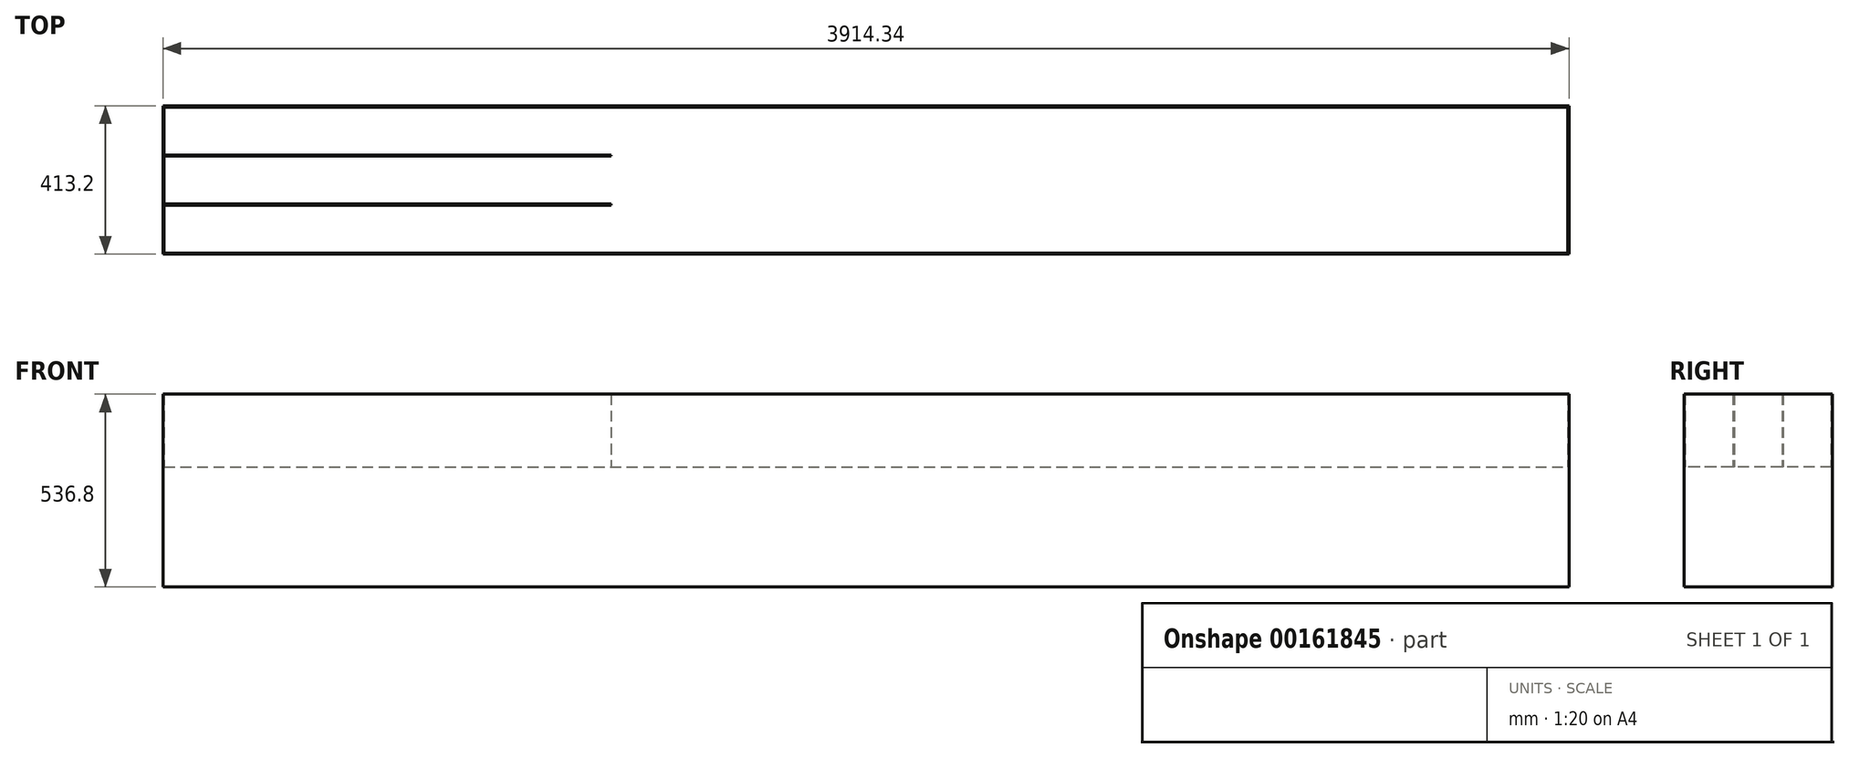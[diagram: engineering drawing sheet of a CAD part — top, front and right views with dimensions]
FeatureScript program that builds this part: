
annotation { "Feature Type Name" : "Feature", "Feature Type Description" : "" }
export const myFeature = defineFeature(function(context is Context, id is Id, definition is map)
    precondition{}
    {
        {
            var Q0;
            Q0=qCreatedBy(makeId("Top.planeOp"),FACE);
            var sketch = newSketch(context, id + "F0", { "sketchPlane" : qUnion([Q0])});
            skLineSegment(sketch, "E0.bottom", {"start": v(-1953.77, 203.2) * mm, "end": v(1953.77, 203.2) * mm});
            skLineSegment(sketch, "E0.top", {"start": v(-1953.77, -203.2) * mm, "end": v(1953.77, -203.2) * mm});
            skLineSegment(sketch, "E0.left", {"start": v(-1953.77, 203.2) * mm, "end": v(-1953.77, -203.2) * mm});
            skLineSegment(sketch, "E0.right", {"start": v(1953.77, 203.2) * mm, "end": v(1953.77, -203.2) * mm});
            skPoint(sketch, "E0.middle", {"position": v(0, 0) * mm});
            skLineSegment(sketch, "E1.bottom", {"start": v(-709.17, 203.2) * mm, "end": v(-705.76, 203.2) * mm});
            skLineSegment(sketch, "E1.top", {"start": v(-709.17, -203.2) * mm, "end": v(-705.76, -203.2) * mm});
            skLineSegment(sketch, "E1.left", {"start": v(-709.17, 203.2) * mm, "end": v(-709.17, -203.2) * mm});
            skLineSegment(sketch, "E1.right", {"start": v(-705.76, 203.2) * mm, "end": v(-705.76, -203.2) * mm});
            skLineSegment(sketch, "E2.bottom", {"start": v(-1953.77, 69.85) * mm, "end": v(-709.17, 69.85) * mm});
            skLineSegment(sketch, "E2.top", {"start": v(-1953.77, 66.45) * mm, "end": v(-709.17, 66.45) * mm});
            skLineSegment(sketch, "E2.left", {"start": v(-1953.77, 69.85) * mm, "end": v(-1953.77, 66.45) * mm});
            skLineSegment(sketch, "E2.right", {"start": v(-709.17, 69.85) * mm, "end": v(-709.17, 66.45) * mm});
            skLineSegment(sketch, "E3.bottom", {"start": v(-1953.77, -66.9) * mm, "end": v(-709.17, -66.9) * mm});
            skLineSegment(sketch, "E3.top", {"start": v(-1953.77, -70.3) * mm, "end": v(-709.17, -70.3) * mm});
            skLineSegment(sketch, "E3.left", {"start": v(-1953.77, -66.9) * mm, "end": v(-1953.77, -70.3) * mm});
            skLineSegment(sketch, "E3.right", {"start": v(-709.17, -66.9) * mm, "end": v(-709.17, -70.3) * mm});
            skLineSegment(sketch, "E4.bottom", {"start": v(-311.15, 203.2) * mm, "end": v(-307.75, 203.2) * mm});
            skLineSegment(sketch, "E4.top", {"start": v(-311.15, -203.2) * mm, "end": v(-307.75, -203.2) * mm});
            skLineSegment(sketch, "E4.left", {"start": v(-311.15, 203.2) * mm, "end": v(-311.15, -203.2) * mm});
            skLineSegment(sketch, "E4.right", {"start": v(-307.75, 203.2) * mm, "end": v(-307.75, -203.2) * mm});
            skLineSegment(sketch, "E5.bottom", {"start": v(-705.76, 0) * mm, "end": v(-311.15, 0) * mm});
            skLineSegment(sketch, "E5.top", {"start": v(-705.76, -3.4) * mm, "end": v(-311.15, -3.4) * mm});
            skLineSegment(sketch, "E5.left", {"start": v(-705.76, 0) * mm, "end": v(-705.76, -3.4) * mm});
            skLineSegment(sketch, "E5.right", {"start": v(-311.15, 0) * mm, "end": v(-311.15, -3.4) * mm});
            skLineSegment(sketch, "E6.bottom", {"start": v(-629.56, 203.2) * mm, "end": v(-626.16, 203.2) * mm});
            skLineSegment(sketch, "E6.top", {"start": v(-629.56, 0) * mm, "end": v(-626.16, 0) * mm});
            skLineSegment(sketch, "E6.left", {"start": v(-629.56, 203.2) * mm, "end": v(-629.56, 0) * mm});
            skLineSegment(sketch, "E6.right", {"start": v(-626.16, 203.2) * mm, "end": v(-626.16, 0) * mm});
            skLineSegment(sketch, "E7.bottom", {"start": v(-629.56, -3.4) * mm, "end": v(-626.16, -3.4) * mm});
            skLineSegment(sketch, "E7.top", {"start": v(-629.56, -203.2) * mm, "end": v(-626.16, -203.2) * mm});
            skLineSegment(sketch, "E7.left", {"start": v(-629.56, -3.4) * mm, "end": v(-629.56, -203.2) * mm});
            skLineSegment(sketch, "E7.right", {"start": v(-626.16, -3.4) * mm, "end": v(-626.16, -203.2) * mm});
            skLineSegment(sketch, "E8.bottom", {"start": v(-549.96, 203.2) * mm, "end": v(-546.56, 203.2) * mm});
            skLineSegment(sketch, "E8.top", {"start": v(-549.96, 0) * mm, "end": v(-546.56, 0) * mm});
            skLineSegment(sketch, "E8.left", {"start": v(-549.96, 203.2) * mm, "end": v(-549.96, 0) * mm});
            skLineSegment(sketch, "E8.right", {"start": v(-546.56, 203.2) * mm, "end": v(-546.56, 0) * mm});
            skLineSegment(sketch, "E9.bottom", {"start": v(-549.96, -3.4) * mm, "end": v(-546.56, -3.4) * mm});
            skLineSegment(sketch, "E9.top", {"start": v(-549.96, -203.2) * mm, "end": v(-546.56, -203.2) * mm});
            skLineSegment(sketch, "E9.left", {"start": v(-549.96, -3.4) * mm, "end": v(-549.96, -203.2) * mm});
            skLineSegment(sketch, "E9.right", {"start": v(-546.56, -3.4) * mm, "end": v(-546.56, -203.2) * mm});
            skLineSegment(sketch, "E10.bottom", {"start": v(-470.36, 203.2) * mm, "end": v(-466.95, 203.2) * mm});
            skLineSegment(sketch, "E10.top", {"start": v(-470.36, 0) * mm, "end": v(-466.95, 0) * mm});
            skLineSegment(sketch, "E10.left", {"start": v(-470.36, 203.2) * mm, "end": v(-470.36, 0) * mm});
            skLineSegment(sketch, "E10.right", {"start": v(-466.95, 203.2) * mm, "end": v(-466.95, 0) * mm});
            skLineSegment(sketch, "E11.bottom", {"start": v(-470.36, -3.4) * mm, "end": v(-466.95, -3.4) * mm});
            skLineSegment(sketch, "E11.top", {"start": v(-470.36, -203.2) * mm, "end": v(-466.95, -203.2) * mm});
            skLineSegment(sketch, "E11.left", {"start": v(-470.36, -3.4) * mm, "end": v(-470.36, -203.2) * mm});
            skLineSegment(sketch, "E11.right", {"start": v(-466.95, -3.4) * mm, "end": v(-466.95, -203.2) * mm});
            skLineSegment(sketch, "E12.bottom", {"start": v(-390.75, 203.2) * mm, "end": v(-387.35, 203.2) * mm});
            skLineSegment(sketch, "E12.top", {"start": v(-390.75, 0) * mm, "end": v(-387.35, 0) * mm});
            skLineSegment(sketch, "E12.left", {"start": v(-390.75, 203.2) * mm, "end": v(-390.75, 0) * mm});
            skLineSegment(sketch, "E12.right", {"start": v(-387.35, 203.2) * mm, "end": v(-387.35, 0) * mm});
            skLineSegment(sketch, "E13.bottom", {"start": v(-390.75, -3.4) * mm, "end": v(-387.35, -3.4) * mm});
            skLineSegment(sketch, "E13.top", {"start": v(-390.75, -203.2) * mm, "end": v(-387.35, -203.2) * mm});
            skLineSegment(sketch, "E13.left", {"start": v(-390.75, -3.4) * mm, "end": v(-390.75, -203.2) * mm});
            skLineSegment(sketch, "E13.right", {"start": v(-387.35, -3.4) * mm, "end": v(-387.35, -203.2) * mm});
            skLineSegment(sketch, "E14.bottom", {"start": v(-307.75, 0) * mm, "end": v(1953.77, 0) * mm});
            skLineSegment(sketch, "E14.top", {"start": v(-307.75, -3.4) * mm, "end": v(1953.77, -3.4) * mm});
            skLineSegment(sketch, "E14.left", {"start": v(-307.75, 0) * mm, "end": v(-307.75, -3.4) * mm});
            skLineSegment(sketch, "E14.right", {"start": v(1953.77, 0) * mm, "end": v(1953.77, -3.4) * mm});
            skLineSegment(sketch, "E15.bottom", {"start": v(-180.75, 203.2) * mm, "end": v(-177.34, 203.2) * mm});
            skLineSegment(sketch, "E15.top", {"start": v(-180.75, 0) * mm, "end": v(-177.34, 0) * mm});
            skLineSegment(sketch, "E15.left", {"start": v(-180.75, 203.2) * mm, "end": v(-180.75, 0) * mm});
            skLineSegment(sketch, "E15.right", {"start": v(-177.34, 203.2) * mm, "end": v(-177.34, 0) * mm});
            skLineSegment(sketch, "E16.bottom", {"start": v(279.86, 203.2) * mm, "end": v(283.26, 203.2) * mm});
            skLineSegment(sketch, "E16.top", {"start": v(279.86, 0) * mm, "end": v(283.26, 0) * mm});
            skLineSegment(sketch, "E16.left", {"start": v(279.86, 203.2) * mm, "end": v(279.86, 0) * mm});
            skLineSegment(sketch, "E16.right", {"start": v(283.26, 203.2) * mm, "end": v(283.26, 0) * mm});
            skLineSegment(sketch, "E17.bottom", {"start": v(562.66, 203.2) * mm, "end": v(566.06, 203.2) * mm});
            skLineSegment(sketch, "E17.top", {"start": v(562.66, 0) * mm, "end": v(566.06, 0) * mm});
            skLineSegment(sketch, "E17.left", {"start": v(562.66, 203.2) * mm, "end": v(562.66, 0) * mm});
            skLineSegment(sketch, "E17.right", {"start": v(566.06, 203.2) * mm, "end": v(566.06, 0) * mm});
            skLineSegment(sketch, "E18.bottom", {"start": v(896.26, 203.2) * mm, "end": v(899.67, 203.2) * mm});
            skLineSegment(sketch, "E18.top", {"start": v(896.26, 0) * mm, "end": v(899.67, 0) * mm});
            skLineSegment(sketch, "E18.left", {"start": v(896.26, 203.2) * mm, "end": v(896.26, 0) * mm});
            skLineSegment(sketch, "E18.right", {"start": v(899.67, 203.2) * mm, "end": v(899.67, 0) * mm});
            skLineSegment(sketch, "E19.bottom", {"start": v(225.65, -3.4) * mm, "end": v(229.06, -3.4) * mm});
            skLineSegment(sketch, "E19.top", {"start": v(225.65, -203.2) * mm, "end": v(229.06, -203.2) * mm});
            skLineSegment(sketch, "E19.left", {"start": v(225.65, -3.4) * mm, "end": v(225.65, -203.2) * mm});
            skLineSegment(sketch, "E19.right", {"start": v(229.06, -3.4) * mm, "end": v(229.06, -203.2) * mm});
            skLineSegment(sketch, "E20.bottom", {"start": v(566.06, -3.4) * mm, "end": v(562.66, -3.4) * mm});
            skLineSegment(sketch, "E20.top", {"start": v(566.06, -203.2) * mm, "end": v(562.66, -203.2) * mm});
            skLineSegment(sketch, "E20.left", {"start": v(566.06, -3.4) * mm, "end": v(566.06, -203.2) * mm});
            skLineSegment(sketch, "E20.right", {"start": v(562.66, -3.4) * mm, "end": v(562.66, -203.2) * mm});
            skLineSegment(sketch, "E21.bottom", {"start": v(896.26, -3.4) * mm, "end": v(899.67, -3.4) * mm});
            skLineSegment(sketch, "E21.top", {"start": v(896.26, -203.2) * mm, "end": v(899.67, -203.2) * mm});
            skLineSegment(sketch, "E21.left", {"start": v(896.26, -3.4) * mm, "end": v(896.26, -203.2) * mm});
            skLineSegment(sketch, "E21.right", {"start": v(899.67, -3.4) * mm, "end": v(899.67, -203.2) * mm});
            skLineSegment(sketch, "E22.bottom", {"start": v(-1957.17, 206.6) * mm, "end": v(1957.17, 206.6) * mm});
            skLineSegment(sketch, "E22.top", {"start": v(-1957.17, -206.6) * mm, "end": v(1957.17, -206.6) * mm});
            skLineSegment(sketch, "E22.left", {"start": v(-1957.17, 206.6) * mm, "end": v(-1957.17, -206.6) * mm});
            skLineSegment(sketch, "E22.right", {"start": v(1957.17, 206.6) * mm, "end": v(1957.17, -206.6) * mm});
            skSolve(sketch);
        }
        {
            var Q0;
            Q0 = qSketchRegion(id + "F0", true);
            var Q1;
            Q1=makeQuery(id+"F0.imprint","IMPRINT",FACE,{"disambiguationData":[TD([[makeQuery(id+"F0.imprint","IMPRINT",EDGE,{"derivedFrom":sQuery(id+"F0.wireOp",EDGE,"E2.bottom")}),-1.0]])]});
            var Q2;
            Q2=makeQuery(id+"F0.imprint","IMPRINT",FACE,{"disambiguationData":[TD([[makeQuery(id+"F0.imprint","IMPRINT",EDGE,{"derivedFrom":sQuery(id+"F0.wireOp",EDGE,"E3.bottom")}),-1.0]])]});
            var Q3;
            {var subQ3=sQuery(id+"F0.wireOp",EDGE,"E1.bottom");Q3=makeQuery(id+"F0.imprint","IMPRINT",FACE,{"disambiguationData":[TD([[makeQuery(id+"F0.imprint","IMPRINT",EDGE,{"derivedFrom":subQ3}),-1.0]])]});}
            var Q4;
            {var subQ7=sQuery(id+"F0.wireOp",EDGE,"E5.left");Q4=makeQuery(id+"F0.imprint","IMPRINT",FACE,{"disambiguationData":[TD([[makeQuery(id+"F0.imprint","IMPRINT",EDGE,{"derivedFrom":subQ7}),1.0]])]});}
            var Q5;
            Q5=makeQuery(id+"F0.imprint","IMPRINT",FACE,{"disambiguationData":[TD([[makeQuery(id+"F0.imprint","IMPRINT",EDGE,{"derivedFrom":sQuery(id+"F0.wireOp",EDGE,"E6.bottom")}),-1.0]])]});
            var Q6;
            Q6=makeQuery(id+"F0.imprint","IMPRINT",FACE,{"disambiguationData":[TD([[makeQuery(id+"F0.imprint","IMPRINT",EDGE,{"derivedFrom":sQuery(id+"F0.wireOp",EDGE,"E7.bottom")}),-1.0]])]});
            var Q7;
            Q7=makeQuery(id+"F0.imprint","IMPRINT",FACE,{"disambiguationData":[TD([[makeQuery(id+"F0.imprint","IMPRINT",EDGE,{"derivedFrom":sQuery(id+"F0.wireOp",EDGE,"E9.bottom")}),-1.0]])]});
            var Q8;
            Q8=makeQuery(id+"F0.imprint","IMPRINT",FACE,{"disambiguationData":[TD([[makeQuery(id+"F0.imprint","IMPRINT",EDGE,{"derivedFrom":sQuery(id+"F0.wireOp",EDGE,"E8.bottom")}),-1.0]])]});
            var Q9;
            Q9=makeQuery(id+"F0.imprint","IMPRINT",FACE,{"disambiguationData":[TD([[makeQuery(id+"F0.imprint","IMPRINT",EDGE,{"derivedFrom":sQuery(id+"F0.wireOp",EDGE,"E10.bottom")}),-1.0]])]});
            var Q10;
            Q10=makeQuery(id+"F0.imprint","IMPRINT",FACE,{"disambiguationData":[TD([[makeQuery(id+"F0.imprint","IMPRINT",EDGE,{"derivedFrom":sQuery(id+"F0.wireOp",EDGE,"E11.bottom")}),-1.0]])]});
            var Q11;
            Q11=makeQuery(id+"F0.imprint","IMPRINT",FACE,{"disambiguationData":[TD([[makeQuery(id+"F0.imprint","IMPRINT",EDGE,{"derivedFrom":sQuery(id+"F0.wireOp",EDGE,"E13.bottom")}),-1.0]])]});
            var Q12;
            Q12=makeQuery(id+"F0.imprint","IMPRINT",FACE,{"disambiguationData":[TD([[makeQuery(id+"F0.imprint","IMPRINT",EDGE,{"derivedFrom":sQuery(id+"F0.wireOp",EDGE,"E12.bottom")}),-1.0]])]});
            var Q13;
            {var subQ5=sQuery(id+"F0.wireOp",EDGE,"E4.bottom");Q13=makeQuery(id+"F0.imprint","IMPRINT",FACE,{"disambiguationData":[TD([[makeQuery(id+"F0.imprint","IMPRINT",EDGE,{"derivedFrom":subQ5}),-1.0]])]});}
            var Q14;
            {var subQ0=sQuery(id+"F0.wireOp",EDGE,"E14.left");Q14=makeQuery(id+"F0.imprint","IMPRINT",FACE,{"disambiguationData":[TD([[makeQuery(id+"F0.imprint","IMPRINT",EDGE,{"derivedFrom":subQ0}),1.0]])]});}
            var Q15;
            Q15=makeQuery(id+"F0.imprint","IMPRINT",FACE,{"disambiguationData":[TD([[makeQuery(id+"F0.imprint","IMPRINT",EDGE,{"derivedFrom":sQuery(id+"F0.wireOp",EDGE,"E15.bottom")}),-1.0]])]});
            var Q16;
            Q16=makeQuery(id+"F0.imprint","IMPRINT",FACE,{"disambiguationData":[TD([[makeQuery(id+"F0.imprint","IMPRINT",EDGE,{"derivedFrom":sQuery(id+"F0.wireOp",EDGE,"E16.bottom")}),-1.0]])]});
            var Q17;
            Q17=makeQuery(id+"F0.imprint","IMPRINT",FACE,{"disambiguationData":[TD([[makeQuery(id+"F0.imprint","IMPRINT",EDGE,{"derivedFrom":sQuery(id+"F0.wireOp",EDGE,"E19.bottom")}),-1.0]])]});
            var Q18;
            Q18=makeQuery(id+"F0.imprint","IMPRINT",FACE,{"disambiguationData":[TD([[makeQuery(id+"F0.imprint","IMPRINT",EDGE,{"derivedFrom":sQuery(id+"F0.wireOp",EDGE,"E20.bottom")}),1.0]])]});
            var Q19;
            Q19=makeQuery(id+"F0.imprint","IMPRINT",FACE,{"disambiguationData":[TD([[makeQuery(id+"F0.imprint","IMPRINT",EDGE,{"derivedFrom":sQuery(id+"F0.wireOp",EDGE,"E17.bottom")}),-1.0]])]});
            var Q20;
            Q20=makeQuery(id+"F0.imprint","IMPRINT",FACE,{"disambiguationData":[TD([[makeQuery(id+"F0.imprint","IMPRINT",EDGE,{"derivedFrom":sQuery(id+"F0.wireOp",EDGE,"E18.bottom")}),-1.0]])]});
            var Q21;
            Q21=makeQuery(id+"F0.imprint","IMPRINT",FACE,{"disambiguationData":[TD([[makeQuery(id+"F0.imprint","IMPRINT",EDGE,{"derivedFrom":sQuery(id+"F0.wireOp",EDGE,"E21.bottom")}),-1.0]])]});
            extrude(context, id + "F1", {"entities" : qUnion([Q0, Q1, Q2, Q3, Q4, Q5, Q6, Q7, Q8, Q9, Q10, Q11, Q12, Q13, Q14, Q15, Q16, Q17, Q18, Q19, Q20, Q21]), "depth" : 533.4 * mm});
        }
        {
            var Q0;
            Q0=makeQuery(id+"F1.opExtrude","CAP_FACE",FACE,{"disambiguationData":[OSD([sQuery(id+"F0.wireOp",EDGE,"E0.bottom"),sQuery(id+"F0.wireOp",EDGE,"E0.top"),sQuery(id+"F0.wireOp",EDGE,"E0.left"),sQuery(id+"F0.wireOp",EDGE,"E0.right"),sQuery(id+"F0.wireOp",EDGE,"E1.left"),sQuery(id+"F0.wireOp",EDGE,"E1.right"),sQuery(id+"F0.wireOp",EDGE,"E2.bottom"),sQuery(id+"F0.wireOp",EDGE,"E2.top"),sQuery(id+"F0.wireOp",EDGE,"E3.bottom"),sQuery(id+"F0.wireOp",EDGE,"E3.top"),sQuery(id+"F0.wireOp",EDGE,"E4.left"),sQuery(id+"F0.wireOp",EDGE,"E4.right"),sQuery(id+"F0.wireOp",EDGE,"E5.bottom"),sQuery(id+"F0.wireOp",EDGE,"E5.top"),sQuery(id+"F0.wireOp",EDGE,"E6.left"),sQuery(id+"F0.wireOp",EDGE,"E6.right"),sQuery(id+"F0.wireOp",EDGE,"E7.left"),sQuery(id+"F0.wireOp",EDGE,"E7.right"),sQuery(id+"F0.wireOp",EDGE,"E8.left"),sQuery(id+"F0.wireOp",EDGE,"E8.right"),sQuery(id+"F0.wireOp",EDGE,"E9.left"),sQuery(id+"F0.wireOp",EDGE,"E9.right"),sQuery(id+"F0.wireOp",EDGE,"E10.left"),sQuery(id+"F0.wireOp",EDGE,"E10.right"),sQuery(id+"F0.wireOp",EDGE,"E11.left"),sQuery(id+"F0.wireOp",EDGE,"E11.right"),sQuery(id+"F0.wireOp",EDGE,"E12.left"),sQuery(id+"F0.wireOp",EDGE,"E12.right"),sQuery(id+"F0.wireOp",EDGE,"E13.left"),sQuery(id+"F0.wireOp",EDGE,"E13.right"),sQuery(id+"F0.wireOp",EDGE,"E14.bottom"),sQuery(id+"F0.wireOp",EDGE,"E14.top"),sQuery(id+"F0.wireOp",EDGE,"E15.left"),sQuery(id+"F0.wireOp",EDGE,"E15.right"),sQuery(id+"F0.wireOp",EDGE,"E16.left"),sQuery(id+"F0.wireOp",EDGE,"E16.right"),sQuery(id+"F0.wireOp",EDGE,"E17.left"),sQuery(id+"F0.wireOp",EDGE,"E17.right"),sQuery(id+"F0.wireOp",EDGE,"E18.left"),sQuery(id+"F0.wireOp",EDGE,"E18.right"),sQuery(id+"F0.wireOp",EDGE,"E19.left"),sQuery(id+"F0.wireOp",EDGE,"E19.right"),sQuery(id+"F0.wireOp",EDGE,"E20.left"),sQuery(id+"F0.wireOp",EDGE,"E20.right"),sQuery(id+"F0.wireOp",EDGE,"E21.left"),sQuery(id+"F0.wireOp",EDGE,"E21.right"),sQuery(id+"F0.wireOp",EDGE,"E22.bottom"),sQuery(id+"F0.wireOp",EDGE,"E22.top"),sQuery(id+"F0.wireOp",EDGE,"E22.left"),sQuery(id+"F0.wireOp",EDGE,"E22.right")])],"isStart":true});
            var sketch = newSketch(context, id + "F2", { "sketchPlane" : qUnion([Q0])});
            skLineSegment(sketch, "E23.bottom", {"start": v(-1957.17, 206.6) * mm, "end": v(1957.17, 206.6) * mm});
            skLineSegment(sketch, "E23.top", {"start": v(-1957.17, -206.6) * mm, "end": v(1957.17, -206.6) * mm});
            skLineSegment(sketch, "E23.left", {"start": v(-1957.17, 206.6) * mm, "end": v(-1957.17, -206.6) * mm});
            skLineSegment(sketch, "E23.right", {"start": v(1957.17, 206.6) * mm, "end": v(1957.17, -206.6) * mm});
            skSolve(sketch);
        }
        {
            var Q0;
            Q0 = qSketchRegion(id + "F2", true);
            extrude(context, id + "F3", {"entities" : qUnion([Q0]), "operationType" : NewBodyOperationType.ADD, "depth" : 3.4 * mm});
        }
        {
            var Q0;
            {var subQ5=sQuery(id+"F0.wireOp",EDGE,"E2.bottom");Q0=makeQuery(id+"F3.boolean.opBoolean","SPLIT",FACE,{"disambiguationData":[TD([makeQuery(id+"F1.opExtrude","SWEPT_FACE",FACE,{"disambiguationData":[OSD([subQ5])]})])],"derivedFrom":makeQuery(id+"F3.opExtrude","CAP_FACE",FACE,{"disambiguationData":[OSD([sQuery(id+"F2.wireOp",EDGE,"E23.bottom"),sQuery(id+"F2.wireOp",EDGE,"E23.top"),sQuery(id+"F2.wireOp",EDGE,"E23.left"),sQuery(id+"F2.wireOp",EDGE,"E23.right")])],"isStart":true})});}
            var Q1;
            {var subQ0=sQuery(id+"F0.wireOp",EDGE,"E2.top");Q1=makeQuery(id+"F3.boolean.opBoolean","SPLIT",FACE,{"disambiguationData":[TD([makeQuery(id+"F1.opExtrude","SWEPT_FACE",FACE,{"disambiguationData":[OSD([subQ0])]})])],"derivedFrom":makeQuery(id+"F3.opExtrude","CAP_FACE",FACE,{"disambiguationData":[OSD([sQuery(id+"F2.wireOp",EDGE,"E23.bottom"),sQuery(id+"F2.wireOp",EDGE,"E23.top"),sQuery(id+"F2.wireOp",EDGE,"E23.left"),sQuery(id+"F2.wireOp",EDGE,"E23.right")])],"isStart":true})});}
            var Q2;
            {var subQ5=sQuery(id+"F0.wireOp",EDGE,"E3.top");Q2=makeQuery(id+"F3.boolean.opBoolean","SPLIT",FACE,{"disambiguationData":[TD([makeQuery(id+"F1.opExtrude","SWEPT_FACE",FACE,{"disambiguationData":[OSD([subQ5])]})])],"derivedFrom":makeQuery(id+"F3.opExtrude","CAP_FACE",FACE,{"disambiguationData":[OSD([sQuery(id+"F2.wireOp",EDGE,"E23.bottom"),sQuery(id+"F2.wireOp",EDGE,"E23.top"),sQuery(id+"F2.wireOp",EDGE,"E23.left"),sQuery(id+"F2.wireOp",EDGE,"E23.right")])],"isStart":true})});}
            var Q3;
            {var subQ3=sQuery(id+"F0.wireOp",EDGE,"E6.left");Q3=makeQuery(id+"F3.boolean.opBoolean","SPLIT",FACE,{"disambiguationData":[TD([makeQuery(id+"F1.opExtrude","SWEPT_FACE",FACE,{"disambiguationData":[OSD([subQ3])]})])],"derivedFrom":makeQuery(id+"F3.opExtrude","CAP_FACE",FACE,{"disambiguationData":[OSD([sQuery(id+"F2.wireOp",EDGE,"E23.bottom"),sQuery(id+"F2.wireOp",EDGE,"E23.top"),sQuery(id+"F2.wireOp",EDGE,"E23.left"),sQuery(id+"F2.wireOp",EDGE,"E23.right")])],"isStart":true})});}
            var Q4;
            {var subQ0=sQuery(id+"F0.wireOp",EDGE,"E6.right");Q4=makeQuery(id+"F3.boolean.opBoolean","SPLIT",FACE,{"disambiguationData":[TD([makeQuery(id+"F1.opExtrude","SWEPT_FACE",FACE,{"disambiguationData":[OSD([subQ0])]})])],"derivedFrom":makeQuery(id+"F3.opExtrude","CAP_FACE",FACE,{"disambiguationData":[OSD([sQuery(id+"F2.wireOp",EDGE,"E23.bottom"),sQuery(id+"F2.wireOp",EDGE,"E23.top"),sQuery(id+"F2.wireOp",EDGE,"E23.left"),sQuery(id+"F2.wireOp",EDGE,"E23.right")])],"isStart":true})});}
            var Q5;
            {var subQ0=sQuery(id+"F0.wireOp",EDGE,"E8.right");Q5=makeQuery(id+"F3.boolean.opBoolean","SPLIT",FACE,{"disambiguationData":[TD([makeQuery(id+"F1.opExtrude","SWEPT_FACE",FACE,{"disambiguationData":[OSD([subQ0])]})])],"derivedFrom":makeQuery(id+"F3.opExtrude","CAP_FACE",FACE,{"disambiguationData":[OSD([sQuery(id+"F2.wireOp",EDGE,"E23.bottom"),sQuery(id+"F2.wireOp",EDGE,"E23.top"),sQuery(id+"F2.wireOp",EDGE,"E23.left"),sQuery(id+"F2.wireOp",EDGE,"E23.right")])],"isStart":true})});}
            var Q6;
            {var subQ0=sQuery(id+"F0.wireOp",EDGE,"E10.right");Q6=makeQuery(id+"F3.boolean.opBoolean","SPLIT",FACE,{"disambiguationData":[TD([makeQuery(id+"F1.opExtrude","SWEPT_FACE",FACE,{"disambiguationData":[OSD([subQ0])]})])],"derivedFrom":makeQuery(id+"F3.opExtrude","CAP_FACE",FACE,{"disambiguationData":[OSD([sQuery(id+"F2.wireOp",EDGE,"E23.bottom"),sQuery(id+"F2.wireOp",EDGE,"E23.top"),sQuery(id+"F2.wireOp",EDGE,"E23.left"),sQuery(id+"F2.wireOp",EDGE,"E23.right")])],"isStart":true})});}
            var Q7;
            {var subQ3=sQuery(id+"F0.wireOp",EDGE,"E12.right");Q7=makeQuery(id+"F3.boolean.opBoolean","SPLIT",FACE,{"disambiguationData":[TD([makeQuery(id+"F1.opExtrude","SWEPT_FACE",FACE,{"disambiguationData":[OSD([subQ3])]})])],"derivedFrom":makeQuery(id+"F3.opExtrude","CAP_FACE",FACE,{"disambiguationData":[OSD([sQuery(id+"F2.wireOp",EDGE,"E23.bottom"),sQuery(id+"F2.wireOp",EDGE,"E23.top"),sQuery(id+"F2.wireOp",EDGE,"E23.left"),sQuery(id+"F2.wireOp",EDGE,"E23.right")])],"isStart":true})});}
            var Q8;
            {var subQ3=sQuery(id+"F0.wireOp",EDGE,"E13.right");Q8=makeQuery(id+"F3.boolean.opBoolean","SPLIT",FACE,{"disambiguationData":[TD([makeQuery(id+"F1.opExtrude","SWEPT_FACE",FACE,{"disambiguationData":[OSD([subQ3])]})])],"derivedFrom":makeQuery(id+"F3.opExtrude","CAP_FACE",FACE,{"disambiguationData":[OSD([sQuery(id+"F2.wireOp",EDGE,"E23.bottom"),sQuery(id+"F2.wireOp",EDGE,"E23.top"),sQuery(id+"F2.wireOp",EDGE,"E23.left"),sQuery(id+"F2.wireOp",EDGE,"E23.right")])],"isStart":true})});}
            var Q9;
            {var subQ0=sQuery(id+"F0.wireOp",EDGE,"E11.right");Q9=makeQuery(id+"F3.boolean.opBoolean","SPLIT",FACE,{"disambiguationData":[TD([makeQuery(id+"F1.opExtrude","SWEPT_FACE",FACE,{"disambiguationData":[OSD([subQ0])]})])],"derivedFrom":makeQuery(id+"F3.opExtrude","CAP_FACE",FACE,{"disambiguationData":[OSD([sQuery(id+"F2.wireOp",EDGE,"E23.bottom"),sQuery(id+"F2.wireOp",EDGE,"E23.top"),sQuery(id+"F2.wireOp",EDGE,"E23.left"),sQuery(id+"F2.wireOp",EDGE,"E23.right")])],"isStart":true})});}
            var Q10;
            {var subQ0=sQuery(id+"F0.wireOp",EDGE,"E9.right");Q10=makeQuery(id+"F3.boolean.opBoolean","SPLIT",FACE,{"disambiguationData":[TD([makeQuery(id+"F1.opExtrude","SWEPT_FACE",FACE,{"disambiguationData":[OSD([subQ0])]})])],"derivedFrom":makeQuery(id+"F3.opExtrude","CAP_FACE",FACE,{"disambiguationData":[OSD([sQuery(id+"F2.wireOp",EDGE,"E23.bottom"),sQuery(id+"F2.wireOp",EDGE,"E23.top"),sQuery(id+"F2.wireOp",EDGE,"E23.left"),sQuery(id+"F2.wireOp",EDGE,"E23.right")])],"isStart":true})});}
            var Q11;
            {var subQ0=sQuery(id+"F0.wireOp",EDGE,"E7.right");Q11=makeQuery(id+"F3.boolean.opBoolean","SPLIT",FACE,{"disambiguationData":[TD([makeQuery(id+"F1.opExtrude","SWEPT_FACE",FACE,{"disambiguationData":[OSD([subQ0])]})])],"derivedFrom":makeQuery(id+"F3.opExtrude","CAP_FACE",FACE,{"disambiguationData":[OSD([sQuery(id+"F2.wireOp",EDGE,"E23.bottom"),sQuery(id+"F2.wireOp",EDGE,"E23.top"),sQuery(id+"F2.wireOp",EDGE,"E23.left"),sQuery(id+"F2.wireOp",EDGE,"E23.right")])],"isStart":true})});}
            var Q12;
            {var subQ3=sQuery(id+"F0.wireOp",EDGE,"E7.left");Q12=makeQuery(id+"F3.boolean.opBoolean","SPLIT",FACE,{"disambiguationData":[TD([makeQuery(id+"F1.opExtrude","SWEPT_FACE",FACE,{"disambiguationData":[OSD([subQ3])]})])],"derivedFrom":makeQuery(id+"F3.opExtrude","CAP_FACE",FACE,{"disambiguationData":[OSD([sQuery(id+"F2.wireOp",EDGE,"E23.bottom"),sQuery(id+"F2.wireOp",EDGE,"E23.top"),sQuery(id+"F2.wireOp",EDGE,"E23.left"),sQuery(id+"F2.wireOp",EDGE,"E23.right")])],"isStart":true})});}
            var Q13;
            {var subQ3=sQuery(id+"F0.wireOp",EDGE,"E19.left");Q13=makeQuery(id+"F3.boolean.opBoolean","SPLIT",FACE,{"disambiguationData":[TD([makeQuery(id+"F1.opExtrude","SWEPT_FACE",FACE,{"disambiguationData":[OSD([subQ3])]})])],"derivedFrom":makeQuery(id+"F3.opExtrude","CAP_FACE",FACE,{"disambiguationData":[OSD([sQuery(id+"F2.wireOp",EDGE,"E23.bottom"),sQuery(id+"F2.wireOp",EDGE,"E23.top"),sQuery(id+"F2.wireOp",EDGE,"E23.left"),sQuery(id+"F2.wireOp",EDGE,"E23.right")])],"isStart":true})});}
            var Q14;
            {var subQ3=sQuery(id+"F0.wireOp",EDGE,"E15.left");Q14=makeQuery(id+"F3.boolean.opBoolean","SPLIT",FACE,{"disambiguationData":[TD([makeQuery(id+"F1.opExtrude","SWEPT_FACE",FACE,{"disambiguationData":[OSD([subQ3])]})])],"derivedFrom":makeQuery(id+"F3.opExtrude","CAP_FACE",FACE,{"disambiguationData":[OSD([sQuery(id+"F2.wireOp",EDGE,"E23.bottom"),sQuery(id+"F2.wireOp",EDGE,"E23.top"),sQuery(id+"F2.wireOp",EDGE,"E23.left"),sQuery(id+"F2.wireOp",EDGE,"E23.right")])],"isStart":true})});}
            var Q15;
            {var subQ0=sQuery(id+"F0.wireOp",EDGE,"E15.right");Q15=makeQuery(id+"F3.boolean.opBoolean","SPLIT",FACE,{"disambiguationData":[TD([makeQuery(id+"F1.opExtrude","SWEPT_FACE",FACE,{"disambiguationData":[OSD([subQ0])]})])],"derivedFrom":makeQuery(id+"F3.opExtrude","CAP_FACE",FACE,{"disambiguationData":[OSD([sQuery(id+"F2.wireOp",EDGE,"E23.bottom"),sQuery(id+"F2.wireOp",EDGE,"E23.top"),sQuery(id+"F2.wireOp",EDGE,"E23.left"),sQuery(id+"F2.wireOp",EDGE,"E23.right")])],"isStart":true})});}
            var Q16;
            {var subQ0=sQuery(id+"F0.wireOp",EDGE,"E16.right");Q16=makeQuery(id+"F3.boolean.opBoolean","SPLIT",FACE,{"disambiguationData":[TD([makeQuery(id+"F1.opExtrude","SWEPT_FACE",FACE,{"disambiguationData":[OSD([subQ0])]})])],"derivedFrom":makeQuery(id+"F3.opExtrude","CAP_FACE",FACE,{"disambiguationData":[OSD([sQuery(id+"F2.wireOp",EDGE,"E23.bottom"),sQuery(id+"F2.wireOp",EDGE,"E23.top"),sQuery(id+"F2.wireOp",EDGE,"E23.left"),sQuery(id+"F2.wireOp",EDGE,"E23.right")])],"isStart":true})});}
            var Q17;
            {var subQ0=sQuery(id+"F0.wireOp",EDGE,"E19.right");Q17=makeQuery(id+"F3.boolean.opBoolean","SPLIT",FACE,{"disambiguationData":[TD([makeQuery(id+"F1.opExtrude","SWEPT_FACE",FACE,{"disambiguationData":[OSD([subQ0])]})])],"derivedFrom":makeQuery(id+"F3.opExtrude","CAP_FACE",FACE,{"disambiguationData":[OSD([sQuery(id+"F2.wireOp",EDGE,"E23.bottom"),sQuery(id+"F2.wireOp",EDGE,"E23.top"),sQuery(id+"F2.wireOp",EDGE,"E23.left"),sQuery(id+"F2.wireOp",EDGE,"E23.right")])],"isStart":true})});}
            extrude(context, id + "F4", {"entities" : qUnion([Q0, Q1, Q2, Q3, Q4, Q5, Q6, Q7, Q8, Q9, Q10, Q11, Q12, Q13, Q14, Q15, Q16, Q17]), "operationType" : NewBodyOperationType.ADD, "depth" : 330.2 * mm});
        }
    });
